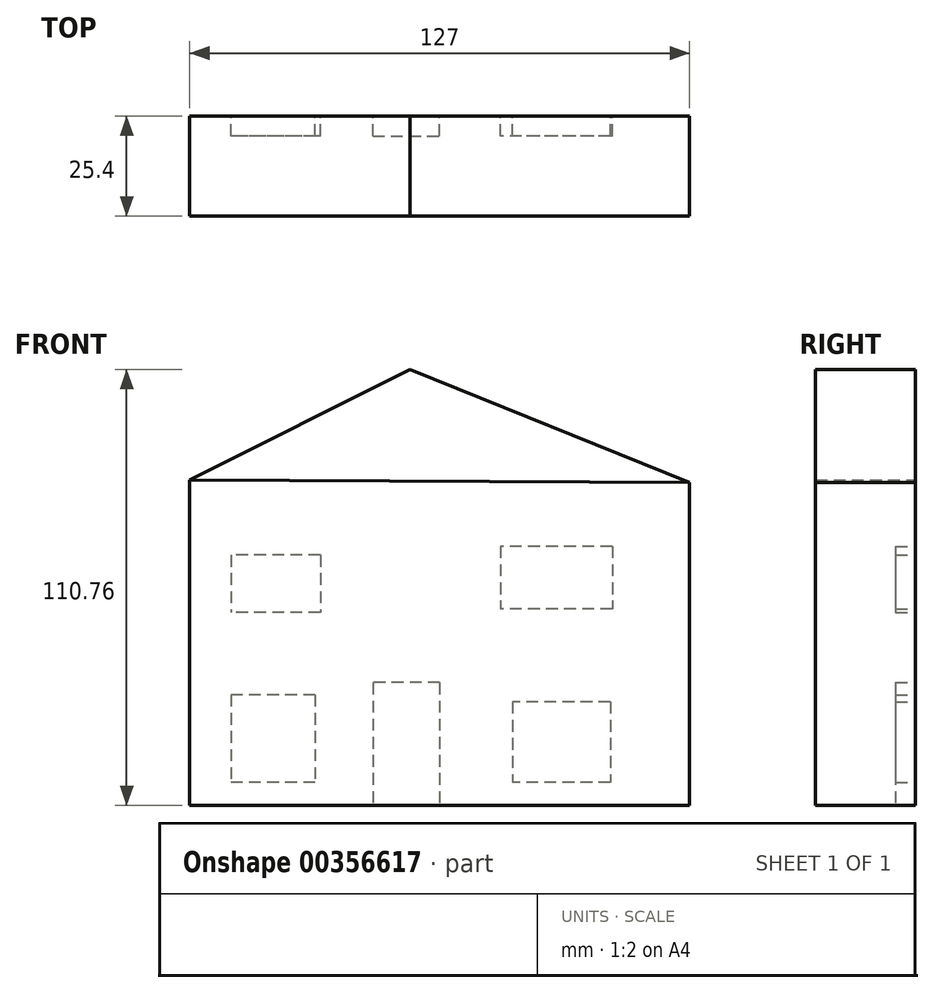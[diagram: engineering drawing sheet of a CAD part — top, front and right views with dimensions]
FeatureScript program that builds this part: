
annotation { "Feature Type Name" : "Feature", "Feature Type Description" : "" }
export const myFeature = defineFeature(function(context is Context, id is Id, definition is map)
    precondition{}
    {
        {
            var Q0;
            Q0=qCreatedBy(makeId("Front.planeOp"),FACE);
            var sketch = newSketch(context, id + "F0", { "sketchPlane" : qUnion([Q0])});
            skLineSegment(sketch, "E0.top", {"start": v(-55.97, -45.21) * mm, "end": v(71.03, -45.21) * mm});
            skLineSegment(sketch, "E0.left", {"start": v(-55.97, 37.5) * mm, "end": v(-55.97, -45.21) * mm});
            skLineSegment(sketch, "E0.right", {"start": v(71.03, 36.84) * mm, "end": v(71.03, -45.21) * mm});
            skLineSegment(sketch, "E1", {"start": v(-55.97, 37.5) * mm, "end": v(71.03, 36.84) * mm});
            skSolve(sketch);
        }
        {
            var Q0;
            Q0=makeQuery(id+"F0.imprint","IMPRINT",FACE,{"disambiguationData":[TD([[makeQuery(id+"F0.imprint","IMPRINT",EDGE,{"derivedFrom":sQuery(id+"F0.wireOp",EDGE,"E0.top")}),1.0]])]});
            var Q1;
            Q1 = qSketchRegion(id + "FSAP8TmCTDFYgYK_1", true);
            extrude(context, id + "F1", {"entities" : qUnion([Q0, Q1]), "depth" : 25.4 * mm});
        }
        {
            var Q0;
            Q0=makeQuery(id+"F1.opExtrude","CAP_FACE",FACE,{"disambiguationData":[OSD([sQuery(id+"F0.wireOp",EDGE,"E0.top"),sQuery(id+"F0.wireOp",EDGE,"E0.left"),sQuery(id+"F0.wireOp",EDGE,"E0.right"),sQuery(id+"F0.wireOp",EDGE,"E1")])],"isStart":true});
            var sketch = newSketch(context, id + "F2", { "sketchPlane" : qUnion([Q0])});
            skLineSegment(sketch, "E2.bottom", {"start": v(-51.36, 20.64) * mm, "end": v(-22.94, 20.64) * mm});
            skLineSegment(sketch, "E2.top", {"start": v(-51.36, 4.66) * mm, "end": v(-22.94, 4.66) * mm});
            skLineSegment(sketch, "E2.left", {"start": v(-51.36, 20.64) * mm, "end": v(-51.36, 4.66) * mm});
            skLineSegment(sketch, "E2.right", {"start": v(-22.94, 20.64) * mm, "end": v(-22.94, 4.66) * mm});
            skLineSegment(sketch, "E3.bottom", {"start": v(22.8, 18.42) * mm, "end": v(45.45, 18.42) * mm});
            skLineSegment(sketch, "E3.top", {"start": v(22.8, 3.77) * mm, "end": v(45.45, 3.77) * mm});
            skLineSegment(sketch, "E3.left", {"start": v(22.8, 18.42) * mm, "end": v(22.8, 3.77) * mm});
            skLineSegment(sketch, "E3.right", {"start": v(45.45, 18.42) * mm, "end": v(45.45, 3.77) * mm});
            skLineSegment(sketch, "E4.bottom", {"start": v(24.14, -17.1) * mm, "end": v(45.45, -17.1) * mm});
            skLineSegment(sketch, "E4.top", {"start": v(24.14, -39.31) * mm, "end": v(45.45, -39.31) * mm});
            skLineSegment(sketch, "E4.left", {"start": v(24.14, -17.1) * mm, "end": v(24.14, -39.31) * mm});
            skLineSegment(sketch, "E4.right", {"start": v(45.45, -17.1) * mm, "end": v(45.45, -39.31) * mm});
            skLineSegment(sketch, "E5.bottom", {"start": v(-50.92, -18.88) * mm, "end": v(-26.05, -18.88) * mm});
            skLineSegment(sketch, "E5.top", {"start": v(-50.92, -39.31) * mm, "end": v(-26.05, -39.31) * mm});
            skLineSegment(sketch, "E5.left", {"start": v(-50.92, -18.88) * mm, "end": v(-50.92, -39.31) * mm});
            skLineSegment(sketch, "E5.right", {"start": v(-26.05, -18.88) * mm, "end": v(-26.05, -39.31) * mm});
            skPoint(sketch, "E6.firstSnap0", {"position": v(-7.53, -45.21) * mm});
            skLineSegment(sketch, "E6.bottom", {"start": v(-7.53, -14) * mm, "end": v(9.48, -14) * mm});
            skLineSegment(sketch, "E6.top", {"start": v(-7.53, -45.21) * mm, "end": v(9.48, -45.21) * mm});
            skLineSegment(sketch, "E6.left", {"start": v(-7.53, -14) * mm, "end": v(-7.53, -45.21) * mm});
            skLineSegment(sketch, "E6.right", {"start": v(9.48, -14) * mm, "end": v(9.48, -45.21) * mm});
            skSolve(sketch);
        }
        {
            var Q0;
            Q0=makeQuery(id+"F2.imprint","IMPRINT",FACE,{"disambiguationData":[TD([[makeQuery(id+"F2.imprint","IMPRINT",EDGE,{"derivedFrom":sQuery(id+"F2.wireOp",EDGE,"E2.bottom")}),-1.0]])]});
            var Q1;
            Q1=makeQuery(id+"F2.imprint","IMPRINT",FACE,{"disambiguationData":[TD([[makeQuery(id+"F2.imprint","IMPRINT",EDGE,{"derivedFrom":sQuery(id+"F2.wireOp",EDGE,"E3.bottom")}),-1.0]])]});
            var Q2;
            Q2=makeQuery(id+"F2.imprint","IMPRINT",FACE,{"disambiguationData":[TD([[makeQuery(id+"F2.imprint","IMPRINT",EDGE,{"derivedFrom":sQuery(id+"F2.wireOp",EDGE,"E4.bottom")}),-1.0]])]});
            var Q3;
            Q3=makeQuery(id+"F2.imprint","IMPRINT",FACE,{"disambiguationData":[TD([[makeQuery(id+"F2.imprint","IMPRINT",EDGE,{"derivedFrom":sQuery(id+"F2.wireOp",EDGE,"E6.bottom")}),-1.0]])]});
            var Q4;
            Q4=makeQuery(id+"F2.imprint","IMPRINT",FACE,{"disambiguationData":[TD([[makeQuery(id+"F2.imprint","IMPRINT",EDGE,{"derivedFrom":sQuery(id+"F2.wireOp",EDGE,"E5.bottom")}),-1.0]])]});
            extrude(context, id + "F3", {"entities" : qUnion([Q0, Q1, Q2, Q3, Q4]), "operationType" : NewBodyOperationType.REMOVE, "oppositeDirection" : true, "depth" : 5.08 * mm});
        }
        {
            var Q0;
            Q0=makeQuery(id+"F1.opExtrude","CAP_FACE",FACE,{"disambiguationData":[OSD([sQuery(id+"F0.wireOp",EDGE,"E0.top"),sQuery(id+"F0.wireOp",EDGE,"E0.left"),sQuery(id+"F0.wireOp",EDGE,"E0.right"),sQuery(id+"F0.wireOp",EDGE,"E1")])],"isStart":true});
            var sketch = newSketch(context, id + "F4", { "sketchPlane" : qUnion([Q0])});
            skLineSegment(sketch, "E7", {"start": v(-71.03, 36.84) * mm, "end": v(0, 65.55) * mm});
            skLineSegment(sketch, "E8", {"start": v(55.97, 37.5) * mm, "end": v(0, 65.55) * mm});
            skSolve(sketch);
        }
        {
            var Q0;
            Q0=makeQuery(id+"F4.imprint","IMPRINT",FACE,{"disambiguationData":[TD([[makeQuery(id+"F4.imprint","IMPRINT",EDGE,{"derivedFrom":sQuery(id+"F4.wireOp",EDGE,"E7")}),-1.0]])]});
            extrude(context, id + "F5", {"entities" : qUnion([Q0]), "oppositeDirection" : true, "depth" : 25.4 * mm});
        }
    });
